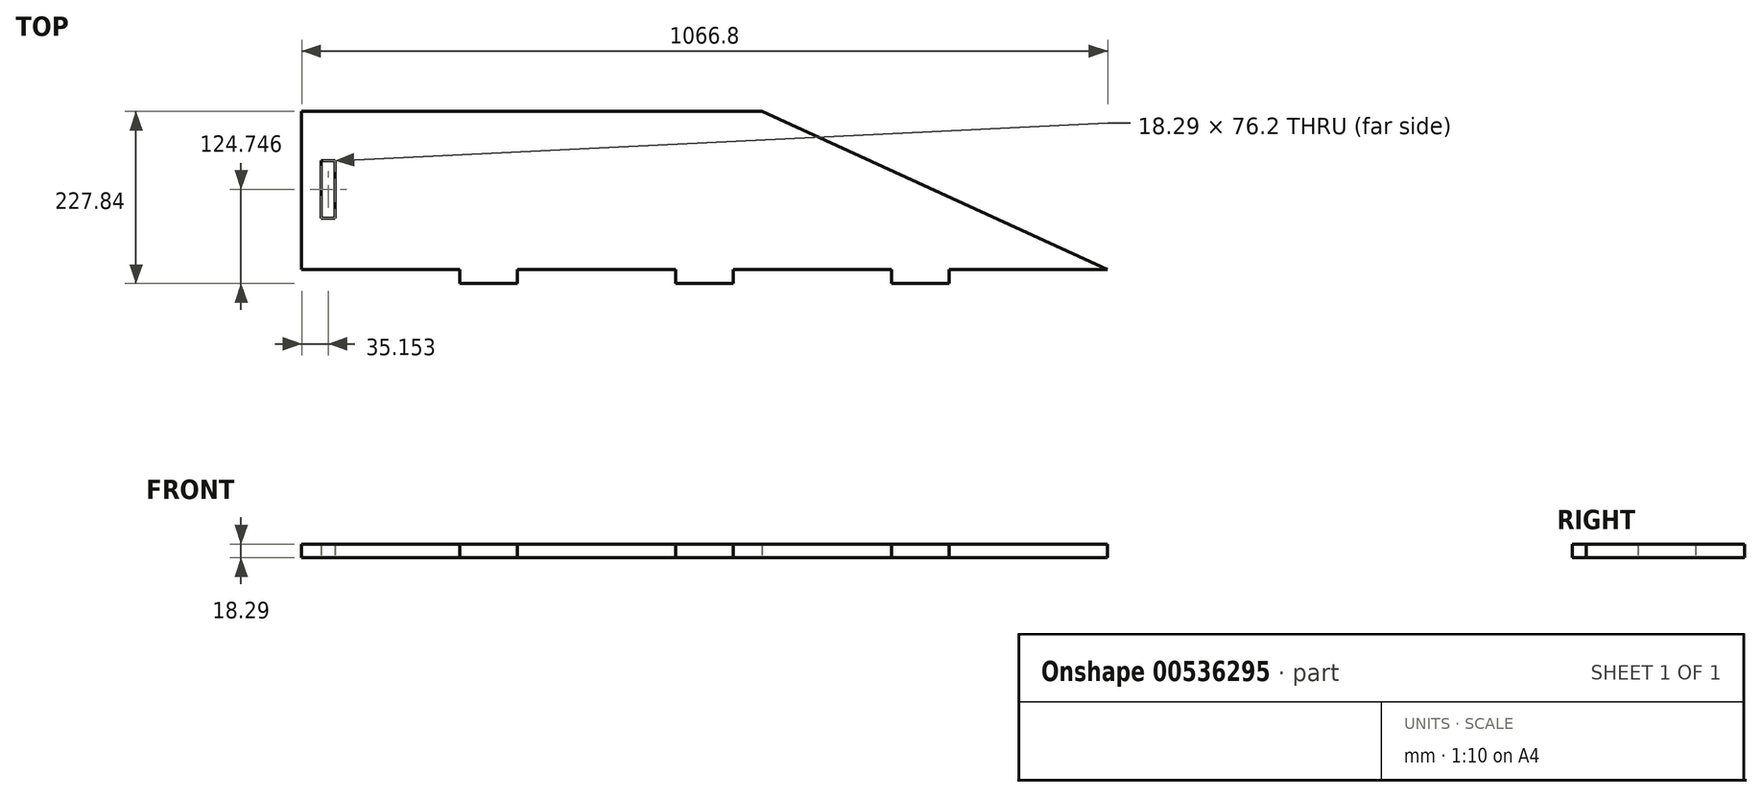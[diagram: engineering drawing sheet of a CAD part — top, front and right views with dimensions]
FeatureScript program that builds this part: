
annotation { "Feature Type Name" : "Feature", "Feature Type Description" : "" }
export const myFeature = defineFeature(function(context is Context, id is Id, definition is map)
    precondition{}
    {
        {
            var Q0;
            Q0=qCreatedBy(makeId("Top.planeOp"),FACE);
            var sketch = newSketch(context, id + "F0", { "sketchPlane" : qUnion([Q0])});
            skLineSegment(sketch, "E0", {"start": v(-1067.61, -32.65) * mm, "end": v(-858.06, -32.65) * mm});
            skLineSegment(sketch, "E1.top", {"start": v(-858.06, -50.94) * mm, "end": v(-781.86, -50.94) * mm});
            skLineSegment(sketch, "E1.left", {"start": v(-858.06, -32.65) * mm, "end": v(-858.06, -50.94) * mm});
            skLineSegment(sketch, "E1.right", {"start": v(-781.86, -32.65) * mm, "end": v(-781.86, -50.94) * mm});
            skLineSegment(sketch, "E2", {"start": v(-781.86, -32.65) * mm, "end": v(-572.31, -32.65) * mm});
            skLineSegment(sketch, "E3.top", {"start": v(-572.31, -50.94) * mm, "end": v(-496.11, -50.94) * mm});
            skLineSegment(sketch, "E3.left", {"start": v(-572.31, -32.65) * mm, "end": v(-572.31, -50.94) * mm});
            skLineSegment(sketch, "E3.right", {"start": v(-496.11, -32.65) * mm, "end": v(-496.11, -50.94) * mm});
            skLineSegment(sketch, "E4", {"start": v(-496.11, -32.65) * mm, "end": v(-286.56, -32.65) * mm});
            skLineSegment(sketch, "E5.top", {"start": v(-286.56, -50.94) * mm, "end": v(-210.36, -50.94) * mm});
            skLineSegment(sketch, "E5.left", {"start": v(-286.56, -32.65) * mm, "end": v(-286.56, -50.94) * mm});
            skLineSegment(sketch, "E5.right", {"start": v(-210.36, -32.65) * mm, "end": v(-210.36, -50.94) * mm});
            skLineSegment(sketch, "E6", {"start": v(-210.36, -32.65) * mm, "end": v(-0.81, -32.65) * mm});
            skLineSegment(sketch, "E7", {"start": v(-1067.61, -32.65) * mm, "end": v(-1067.61, 176.9) * mm});
            skLineSegment(sketch, "E8", {"start": v(-1067.61, 176.9) * mm, "end": v(-458.01, 176.9) * mm});
            skLineSegment(sketch, "E9", {"start": v(-458.01, 176.9) * mm, "end": v(-0.81, -32.65) * mm});
            skSolve(sketch);
        }
        {
            var Q0;
            Q0=makeQuery(id+"F0.imprint","IMPRINT",FACE,{"disambiguationData":[TD([[makeQuery(id+"F0.imprint","IMPRINT",EDGE,{"derivedFrom":sQuery(id+"F0.wireOp",EDGE,"E0")}),1.0]])]});
            extrude(context, id + "F1", {"entities" : qUnion([Q0]), "depth" : 18.29 * mm, "offsetDistance" : 25.4 * mm});
        }
        {
            var Q0;
            Q0=qCreatedBy(makeId("Top.planeOp"),FACE);
            var sketch = newSketch(context, id + "F2", { "sketchPlane" : qUnion([Q0])});
            skLineSegment(sketch, "E10", {"start": v(-1067, -29.72) * mm, "end": v(-1067, 27.82) * mm});
            skLineSegment(sketch, "E11", {"start": v(-1067.81, 177.16) * mm, "end": v(-1067, 111.6) * mm});
            skLineSegment(sketch, "E12.bottom", {"start": v(-1041.6, 111.9) * mm, "end": v(-1023.31, 111.9) * mm});
            skLineSegment(sketch, "E12.top", {"start": v(-1041.6, 35.7) * mm, "end": v(-1023.31, 35.7) * mm});
            skLineSegment(sketch, "E12.left", {"start": v(-1041.6, 111.9) * mm, "end": v(-1041.6, 35.7) * mm});
            skLineSegment(sketch, "E12.right", {"start": v(-1023.31, 111.9) * mm, "end": v(-1023.31, 35.7) * mm});
            skSolve(sketch);
        }
        {
            var Q0;
            Q0 = qSketchRegion(id + "F2", true);
            extrude(context, id + "F3", {"entities" : qUnion([Q0]), "operationType" : NewBodyOperationType.REMOVE, "depth" : 25.4 * mm, "offsetDistance" : 25.4 * mm});
        }
    });
